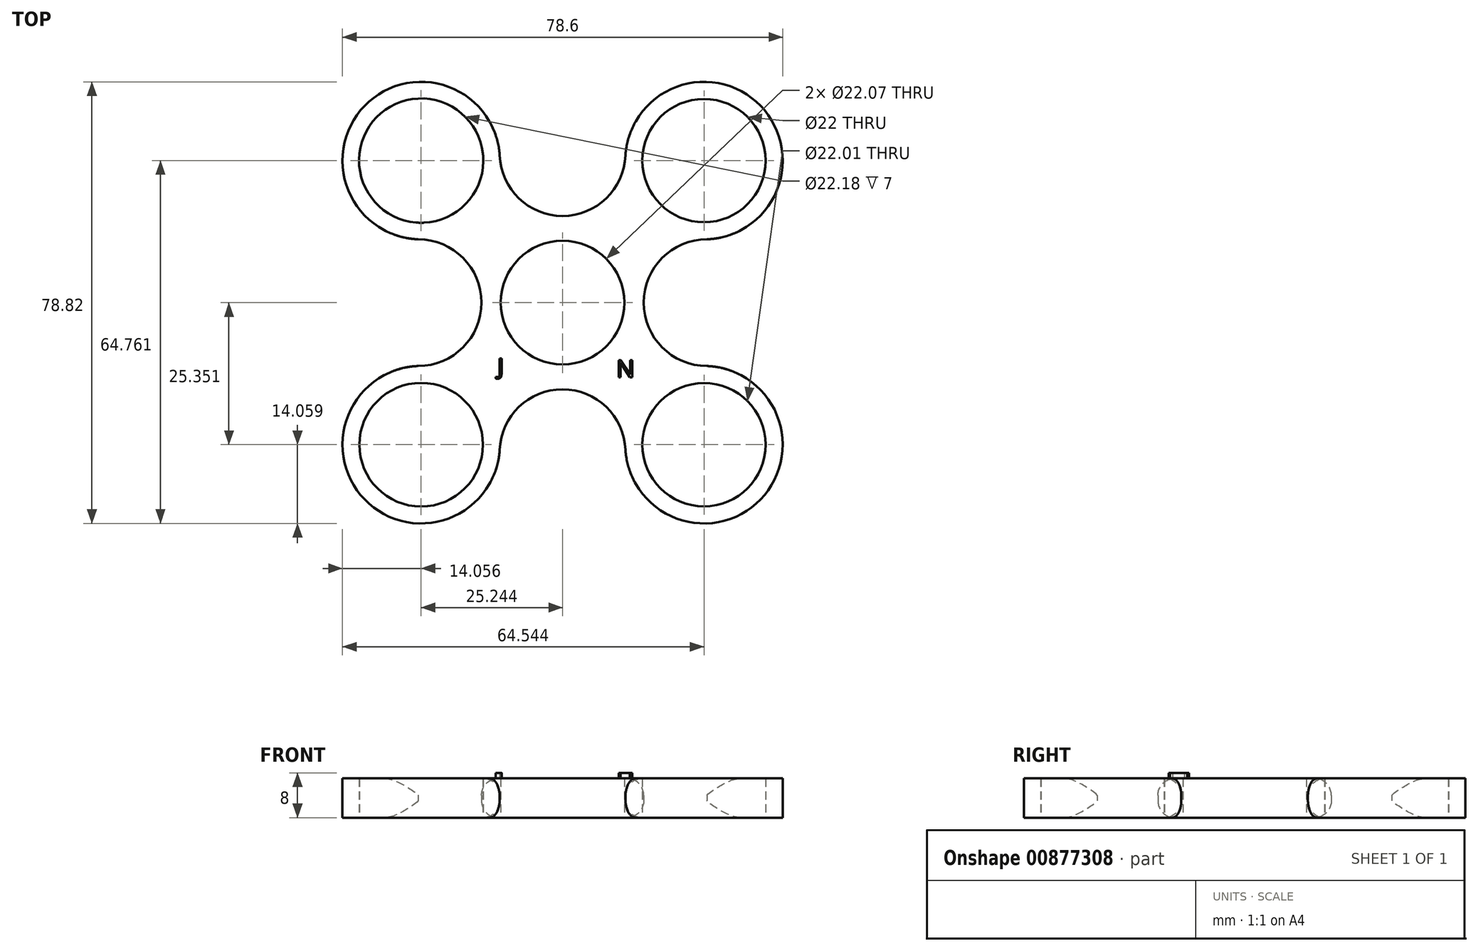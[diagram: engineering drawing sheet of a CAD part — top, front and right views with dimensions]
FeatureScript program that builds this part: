
annotation { "Feature Type Name" : "Feature", "Feature Type Description" : "" }
export const myFeature = defineFeature(function(context is Context, id is Id, definition is map)
    precondition{}
    {
        {
            var Q0;
            Q0=qCreatedBy(makeId("Top.planeOp"),FACE);
            var sketch = newSketch(context, id + "F0", { "sketchPlane" : qUnion([Q0])});
            skArc(sketch, "E0.MirrorCS", {"start": v(-11.22, 26.28) * mm, "mid": v(-7.8, 18.62) * mm, "end": v(0, 15.47) * mm});
            skArc(sketch, "E1.MirrorCS", {"start": v(11.22, 26.28) * mm, "mid": v(7.8, 18.62) * mm, "end": v(0, 15.47) * mm});
            skArc(sketch, "E2.MirrorCS", {"start": v(11.22, -26.28) * mm, "mid": v(7.8, -18.62) * mm, "end": v(0, -15.47) * mm});
            skArc(sketch, "E3", {"start": v(-11.22, 26.28) * mm, "mid": v(-35.33, 35.14) * mm, "end": v(-25.77, 11.3) * mm});
            skArc(sketch, "E4.MirrorCS", {"start": v(-11.22, -26.28) * mm, "mid": v(-35.33, -35.14) * mm, "end": v(-25.77, -11.3) * mm});
            skArc(sketch, "E5.MirrorCS", {"start": v(-11.22, -26.28) * mm, "mid": v(-7.8, -18.62) * mm, "end": v(0, -15.47) * mm});
            skArc(sketch, "E6.MirrorCS", {"start": v(11.22, 26.28) * mm, "mid": v(35.33, 35.14) * mm, "end": v(25.77, 11.3) * mm});
            skArc(sketch, "E7.MirrorCS", {"start": v(11.22, -26.28) * mm, "mid": v(35.33, -35.14) * mm, "end": v(25.77, -11.3) * mm});
            skLineSegment(sketch, "E8", {"start": v(-25.24, 25.35) * mm, "end": v(0, 0) * mm});
            skLineSegment(sketch, "E9", {"start": v(0, 0) * mm, "end": v(25.24, 25.35) * mm});
            skLineSegment(sketch, "E10", {"start": v(0, 0) * mm, "end": v(25.24, -25.35) * mm});
            skLineSegment(sketch, "E11", {"start": v(0, 0) * mm, "end": v(-25.24, -25.35) * mm});
            skCircle(sketch, "E12", {"center": v(-25.24, 25.35) * mm, "radius": 11.1 * mm});
            skCircle(sketch, "E13", {"center": v(25.24, 25.35) * mm, "radius": 11 * mm});
            skCircle(sketch, "E14", {"center": v(25.24, -25.35) * mm, "radius": 11 * mm});
            skCircle(sketch, "E15", {"center": v(-25.24, -25.35) * mm, "radius": 11.03 * mm});
            skCircle(sketch, "E16", {"center": v(0, 0) * mm, "radius": 11.04 * mm});
            skArc(sketch, "E17", {"start": v(-25.77, -11.3) * mm, "mid": v(-14.48, 0) * mm, "end": v(-25.77, 11.3) * mm});
            skArc(sketch, "E18.MirrorCS", {"start": v(25.77, -11.3) * mm, "mid": v(14.48, 0) * mm, "end": v(25.77, 11.3) * mm});
            skSolve(sketch);
        }
        {
            var Q0;
            Q0 = qSketchRegion(id + "F0", true);
            var Q1;
            Q1=sQuery(id+"F0.wireOp",EDGE,"E3");
            var Q2;
            Q2=sQuery(id+"F0.wireOp",EDGE,"E0.MirrorCS");
            var Q3;
            Q3=sQuery(id+"F0.wireOp",EDGE,"E1.MirrorCS");
            var Q4;
            Q4=sQuery(id+"F0.wireOp",EDGE,"E6.MirrorCS");
            var Q5;
            Q5=sQuery(id+"F0.wireOp",EDGE,"733de236-dd0d-40ed-9bf9-e7e08540270b1.MirrorCS");
            var Q6;
            Q6=sQuery(id+"F0.wireOp",EDGE,"E7.MirrorCS");
            var Q7;
            Q7=sQuery(id+"F0.wireOp",EDGE,"E2.MirrorCS");
            var Q8;
            Q8=sQuery(id+"F0.wireOp",EDGE,"E5.MirrorCS");
            var Q9;
            Q9=sQuery(id+"F0.wireOp",EDGE,"E4.MirrorCS");
            var Q10;
            Q10=sQuery(id+"F0.wireOp",EDGE,"6a7b4505-81e8-4474-8d76-1a185cc327733.MirrorCS");
            extrude(context, id + "F1", {"entities" : qUnion([Q0]), "surfaceEntities" : qUnion([Q1, Q2, Q3, Q4, Q5, Q6, Q7, Q8, Q9, Q10]), "depth" : 7 * mm, "offsetDistance" : 25 * mm});
        }
        {
            var Q0;
            Q0=makeQuery(id+"F1.opExtrude","CAP_EDGE",EDGE,{"disambiguationData":[OSD([sQuery(id+"F0.wireOp",EDGE,"E0.MirrorCS"),sQuery(id+"F0.wireOp",EDGE,"E1.MirrorCS")])],"isStart":false});
            var Q1;
            Q1=makeQuery(id+"F1.opExtrude","CAP_EDGE",EDGE,{"disambiguationData":[OSD([sQuery(id+"F0.wireOp",EDGE,"E17")])],"isStart":false});
            var Q2;
            Q2=makeQuery(id+"F1.opExtrude","CAP_EDGE",EDGE,{"disambiguationData":[OSD([sQuery(id+"F0.wireOp",EDGE,"E2.MirrorCS"),sQuery(id+"F0.wireOp",EDGE,"E5.MirrorCS")])],"isStart":false});
            var Q3;
            Q3=makeQuery(id+"F1.opExtrude","CAP_EDGE",EDGE,{"disambiguationData":[OSD([sQuery(id+"F0.wireOp",EDGE,"E18.MirrorCS")])],"isStart":true});
            var Q4;
            Q4=makeQuery(id+"F1.opExtrude","CAP_EDGE",EDGE,{"disambiguationData":[OSD([sQuery(id+"F0.wireOp",EDGE,"E18.MirrorCS")])],"isStart":false});
            var Q5;
            Q5=makeQuery(id+"F1.opExtrude","CAP_EDGE",EDGE,{"disambiguationData":[OSD([sQuery(id+"F0.wireOp",EDGE,"E2.MirrorCS"),sQuery(id+"F0.wireOp",EDGE,"E5.MirrorCS")])],"isStart":true});
            var Q6;
            Q6=makeQuery(id+"F1.opExtrude","CAP_EDGE",EDGE,{"disambiguationData":[OSD([sQuery(id+"F0.wireOp",EDGE,"E17")])],"isStart":true});
            var Q7;
            Q7=makeQuery(id+"F1.opExtrude","CAP_EDGE",EDGE,{"disambiguationData":[OSD([sQuery(id+"F0.wireOp",EDGE,"E0.MirrorCS"),sQuery(id+"F0.wireOp",EDGE,"E1.MirrorCS")])],"isStart":true});
            fillet(context, id + "F2", {"entities" : qUnion([Q0, Q1, Q2, Q3, Q4, Q5, Q6, Q7]), "radius" : 3 * mm, "tangentPropagation" : true, "allowEdgeOverflow" : false});
        }
        {
            var Q0;
            Q0=makeQuery(id+"F2.opFillet","SPLIT",FACE,{"disambiguationData":[OD(0.0)],"derivedFrom":makeQuery(id+"F1.opExtrude","CAP_FACE",FACE,{"disambiguationData":[OSD([sQuery(id+"F0.wireOp",EDGE,"E0.MirrorCS"),sQuery(id+"F0.wireOp",EDGE,"E1.MirrorCS"),sQuery(id+"F0.wireOp",EDGE,"E2.MirrorCS"),sQuery(id+"F0.wireOp",EDGE,"E3"),sQuery(id+"F0.wireOp",EDGE,"E4.MirrorCS"),sQuery(id+"F0.wireOp",EDGE,"E5.MirrorCS"),sQuery(id+"F0.wireOp",EDGE,"E6.MirrorCS"),sQuery(id+"F0.wireOp",EDGE,"E7.MirrorCS"),sQuery(id+"F0.wireOp",EDGE,"E12"),sQuery(id+"F0.wireOp",EDGE,"E13"),sQuery(id+"F0.wireOp",EDGE,"E14"),sQuery(id+"F0.wireOp",EDGE,"E15"),sQuery(id+"F0.wireOp",EDGE,"E16"),sQuery(id+"F0.wireOp",EDGE,"E17"),sQuery(id+"F0.wireOp",EDGE,"E18.MirrorCS")])],"isStart":false})});
            var sketch = newSketch(context, id + "F3", { "sketchPlane" : qUnion([Q0])});
            skText(sketch, "E19", { "text": "J", "fontName": "OpenSans-Regular.ttf"});
            skText(sketch, "E20", { "text": "N", "fontName": "OpenSans-Regular.ttf"});
            const initialGuessF3  = {"E19": [-0.0116, -0.01282, 1, 0, 0.0029], "E20": [0.00958, -0.01334, 1, 0, 0.00312]};
            skSetInitialGuess(sketch, initialGuessF3);
            skSolve(sketch);
        }
        {
            var Q0;
            Q0 = qSketchRegion(id + "F3", true);
            extrude(context, id + "F4", {"entities" : qUnion([Q0]), "operationType" : NewBodyOperationType.ADD, "depth" : 1 * mm, "offsetDistance" : 25 * mm});
        }
    });
